# Revit family: led_e_t5_batten_600_9w_s_4000k__bl_140044076
name_source: partatom
category: Leuchten
revit_build: Autodesk Revit 2016 (Build: 20190508_0715(x64)
units: mm (PartAtom-declared; Revit-internal decimal feet)

## family parameters
Basisbauteil = Fläche
Beim Laden mit Abzugskörper schneiden = Nein
Bemaßung runder Anschluss = Durchmesser verwenden
Gemeinsam genutzt = Nein
Lichtquelle = Nein
Raumberechnungspunkt = Nein
Teiletyp = Normal

## types (1)
- LED E T5 batten 600 9W S 4000K  BL (1 x LED, 950 lm)
    Approval mark = CE
    Beschreibung = Linear LED batten with power switch. Uniform, diffused light, creating a pleasant atmosphere. Battens connect up to 15 meters. Including power cable, mounting and connection pieces (fixed and flexible). Including integrated switch. Energy saving up to 50%. Free to position stainless steel mounting clips.
    CIE Flux Codes = 39 67 87 86 100
    Control Gear = Electronic ballast
    Height = 35 mm
    Hersteller = OPPLE
    Lamp Light Flux = 950 lm
    Lamp count = 1
    Lampe = 1 x LED
    Length = 600 mm
    Luminous efficacy = 105 lm/W
    ModVariant = Nein
    Modell = 140044076
    Mounting Place = Wall
    Mounting Type = Surface mounted
    Number of Poles = 1
    OnlyDefault = Ja
    Power Factor = 1
    Product Name = LED E T5 batten 600 9W S 4000K  BL
    Product group = T5 Batten S with switch
    ProductGroupID = 2011
    Protection Class = Protection class I
    Protection Degree = IP 20
    RLX_Detail_Level = 1
    RlxData = <blob elided: 28773 chars, md5=0b225fb7>
    Scheinlast = 9 VA
    Socket = socket
    Standby Power = 0 W
    System Light Flux = 949 lm
    System Power = 9 W
    Typenbild = 140044076.jpg
    Typenkommentare = Product without accessories
    URL = http://relux.com
    VarID = ---
    Voltage = 0 V
    Vorgabe-Ansicht = 1800 mm
    Weight = 0.00 kg
    Width = 22 mm

## geometry (parser evidence)
native form markers: Blend x4, Sweep x13
no freeform markers — native parametric forms only
